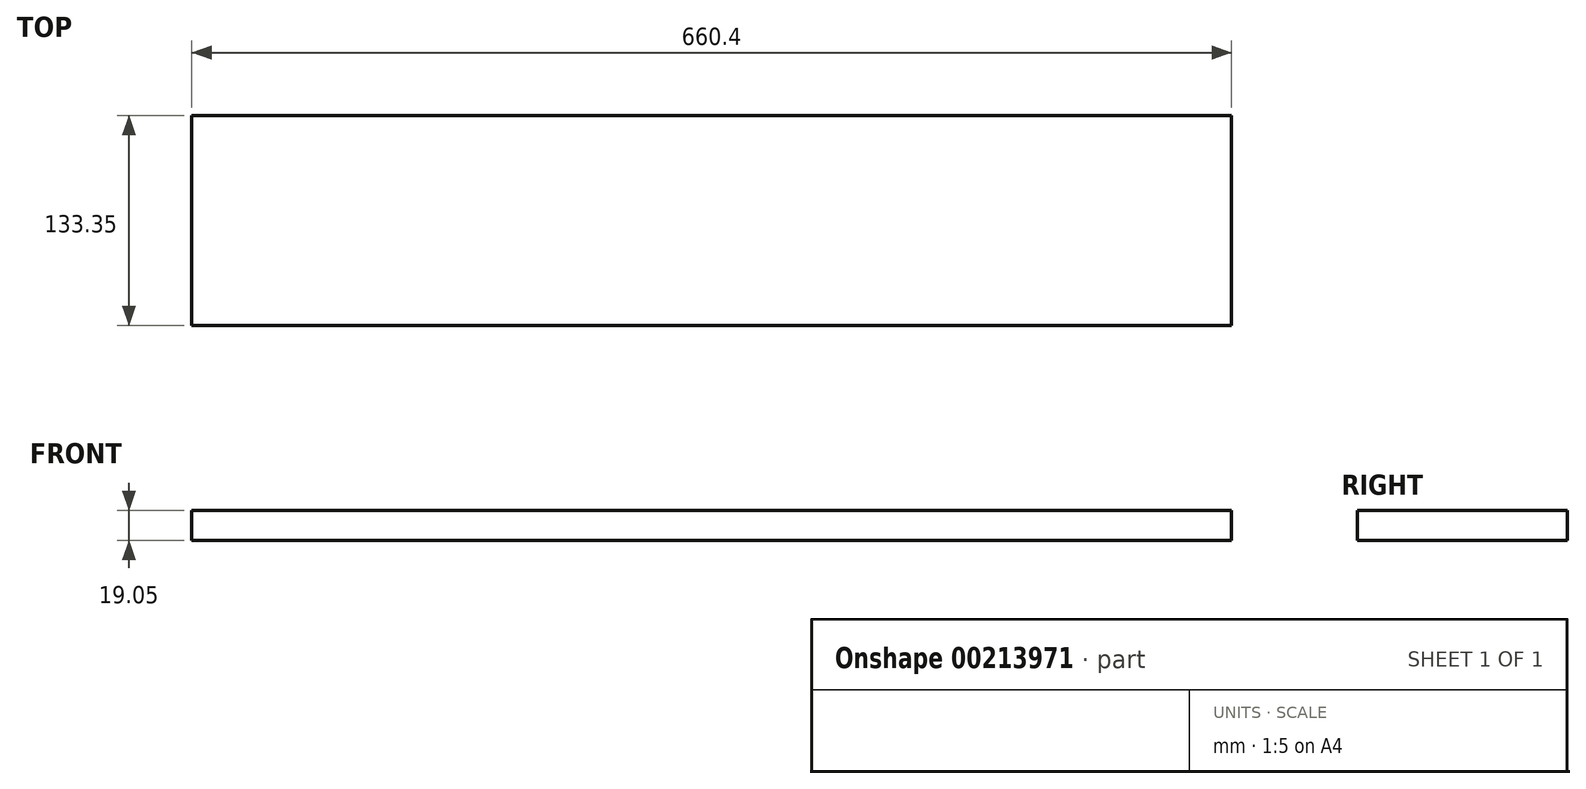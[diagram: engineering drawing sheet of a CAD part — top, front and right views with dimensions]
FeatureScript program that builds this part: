
annotation { "Feature Type Name" : "Feature", "Feature Type Description" : "" }
export const myFeature = defineFeature(function(context is Context, id is Id, definition is map)
    precondition{}
    {
        {
            var Q0;
            Q0=qCreatedBy(makeId("Front.planeOp"),FACE);
            var sketch = newSketch(context, id + "F0", { "sketchPlane" : qUnion([Q0])});
            skLineSegment(sketch, "E0.bottom", {"start": v(-330.2, 19.05) * mm, "end": v(330.2, 19.05) * mm});
            skLineSegment(sketch, "E0.top", {"start": v(-330.2, 0) * mm, "end": v(330.2, 0) * mm});
            skLineSegment(sketch, "E0.left", {"start": v(-330.2, 19.05) * mm, "end": v(-330.2, 0) * mm});
            skLineSegment(sketch, "E0.right", {"start": v(330.2, 19.05) * mm, "end": v(330.2, 0) * mm});
            skSolve(sketch);
        }
        {
            var Q0;
            Q0=makeQuery(id+"F0.imprint","IMPRINT",FACE,{"disambiguationData":[TD([[makeQuery(id+"F0.imprint","IMPRINT",EDGE,{"derivedFrom":sQuery(id+"F0.wireOp",EDGE,"E0.bottom")}),-1.0]])]});
            extrude(context, id + "F1", {"entities" : qUnion([Q0]), "depth" : 133.35 * mm});
        }
    });
